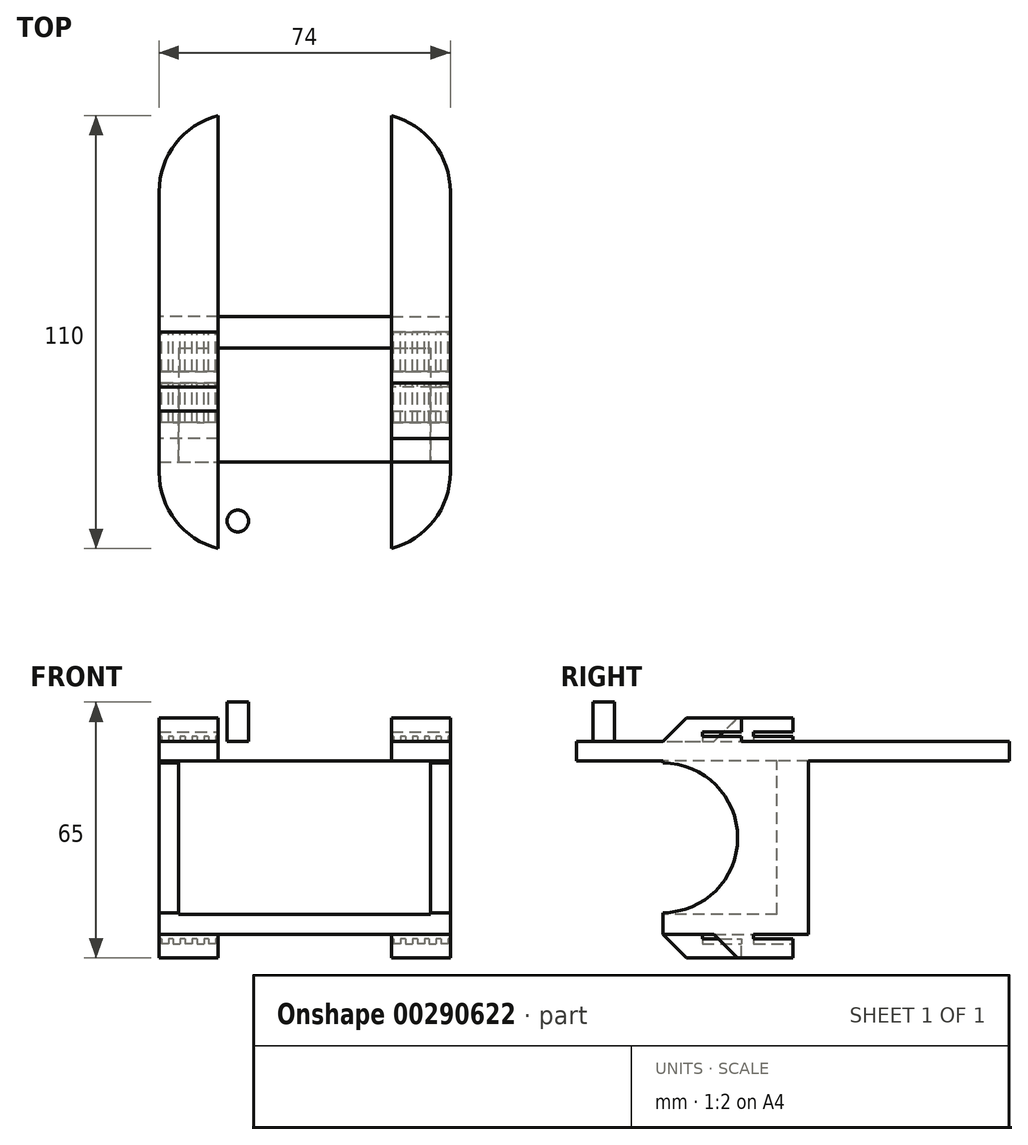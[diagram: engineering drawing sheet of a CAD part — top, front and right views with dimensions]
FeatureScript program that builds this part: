
annotation { "Feature Type Name" : "Feature", "Feature Type Description" : "" }
export const myFeature = defineFeature(function(context is Context, id is Id, definition is map)
    precondition{}
    {
        {
            var Q0;
            Q0=qCreatedBy(makeId("Top.planeOp"),FACE);
            var sketch = newSketch(context, id + "F0", { "sketchPlane" : qUnion([Q0])});
            skLineSegment(sketch, "E0.bottom", {"start": v(-22, 55) * mm, "end": v(22, 55) * mm});
            skLineSegment(sketch, "E0.top", {"start": v(-22, -55) * mm, "end": v(22, -55) * mm});
            skLineSegment(sketch, "E0.left", {"start": v(-22, 55) * mm, "end": v(-22, -55) * mm});
            skLineSegment(sketch, "E0.right", {"start": v(22, 55) * mm, "end": v(22, -55) * mm});
            skLineSegment(sketch, "E1", {"start": v(-22, 0) * mm, "end": v(22, 0) * mm, "construction": true});
            skLineSegment(sketch, "E2", {"start": v(0, 55) * mm, "end": v(0, 25) * mm});
            skPoint(sketch, "E2.endSnap0", {"position": v(0, 55) * mm});
            skLineSegment(sketch, "E3", {"start": v(0, -55) * mm, "end": v(0, -25) * mm});
            skPoint(sketch, "E3.endSnap0", {"position": v(0, -55) * mm});
            skCircle(sketch, "E4", {"center": v(-17, 48) * mm, "radius": 2.75 * mm});
            skLineSegment(sketch, "E5", {"start": v(-22, 30) * mm, "end": v(22, 30) * mm, "construction": true});
            skCircle(sketch, "E6.MirrorC", {"center": v(17, 48) * mm, "radius": 2.75 * mm});
            skCircle(sketch, "E7.MirrorC", {"center": v(-17, 12) * mm, "radius": 2.75 * mm});
            skCircle(sketch, "E8.MirrorC", {"center": v(17, 12) * mm, "radius": 2.75 * mm});
            skCircle(sketch, "E9.MirrorC", {"center": v(-17, -12) * mm, "radius": 2.75 * mm});
            skCircle(sketch, "E10.MirrorC", {"center": v(17, -12) * mm, "radius": 2.75 * mm});
            skCircle(sketch, "E11.MirrorC", {"center": v(17, -48) * mm, "radius": 2.75 * mm});
            skCircle(sketch, "E12.MirrorC", {"center": v(-17, -48) * mm, "radius": 2.75 * mm});
            skSolve(sketch);
        }
        {
            var Q0;
            Q0 = qSketchRegion(id + "F0", true);
            extrude(context, id + "F1", {"entities" : qUnion([Q0]), "depth" : 5 * mm});
        }
        {
            var Q0;
            Q0=makeQuery(id+"F1.opExtrude","CAP_FACE",FACE,{"disambiguationData":[OSD([sQuery(id+"F0.wireOp",EDGE,"E0.bottom"),sQuery(id+"F0.wireOp",EDGE,"E0.top"),sQuery(id+"F0.wireOp",EDGE,"E0.left"),sQuery(id+"F0.wireOp",EDGE,"E0.right")])],"isStart":false});
            var sketch = newSketch(context, id + "F2", { "sketchPlane" : qUnion([Q0])});
            skLineSegment(sketch, "E13.bottom", {"start": v(22, -13) * mm, "end": v(37, -13) * mm});
            skLineSegment(sketch, "E13.top", {"start": v(22, -33) * mm, "end": v(37, -33) * mm});
            skLineSegment(sketch, "E13.left", {"start": v(22, -13) * mm, "end": v(22, -33) * mm});
            skLineSegment(sketch, "E13.right", {"start": v(37, -13) * mm, "end": v(37, -33) * mm});
            skPoint(sketch, "E14.start.orphan", {"position": v(22, 0) * mm});
            skSolve(sketch);
        }
        {
            var Q0;
            Q0 = qSketchRegion(id + "F2", true);
            extrude(context, id + "F3", {"entities" : qUnion([Q0]), "depth" : 6 * mm});
        }
        {
            var Q0;
            Q0=makeQuery(id+"F3.opExtrude","CAP_FACE",FACE,{"disambiguationData":[OSD([sQuery(id+"F2.wireOp",EDGE,"E13.bottom"),sQuery(id+"F2.wireOp",EDGE,"E13.top"),sQuery(id+"F2.wireOp",EDGE,"E13.left"),sQuery(id+"F2.wireOp",EDGE,"E13.right")])],"isStart":true});
            extrude(context, id + "F4", {"entities" : qUnion([Q0]), "operationType" : NewBodyOperationType.ADD, "depth" : 5 * mm});
        }
        {
            var Q0;
            Q0=qCreatedBy(makeId("Top.planeOp"),FACE);
            var sketch = newSketch(context, id + "F5", { "sketchPlane" : qUnion([Q0])});
            skLineSegment(sketch, "E15.bottom", {"start": v(-37, 0) * mm, "end": v(-22, 0) * mm});
            skLineSegment(sketch, "E15.top", {"start": v(-37, -20) * mm, "end": v(-22, -20) * mm});
            skLineSegment(sketch, "E15.left", {"start": v(-37, 0) * mm, "end": v(-37, -20) * mm});
            skLineSegment(sketch, "E15.right", {"start": v(-22, 0) * mm, "end": v(-22, -20) * mm});
            skSolve(sketch);
        }
        {
            var Q0;
            Q0=makeQuery(id+"F5.imprint","IMPRINT",FACE,{"disambiguationData":[TD([[makeQuery(id+"F5.imprint","IMPRINT",EDGE,{"derivedFrom":sQuery(id+"F5.wireOp",EDGE,"E15.bottom")}),-1.0]])]});
            extrude(context, id + "F6", {"entities" : qUnion([Q0]), "operationType" : NewBodyOperationType.ADD, "depth" : 11 * mm});
        }
        {
            var Q0;
            Q0=makeQuery(id+"F6.opExtrude","SWEPT_FACE",FACE,{"disambiguationData":[OSD([sQuery(id+"F5.wireOp",EDGE,"E15.bottom")])]});
            var sketch = newSketch(context, id + "F7", { "sketchPlane" : qUnion([Q0])});
            skPoint(sketch, "E16.start.orphan", {"position": v(22, 6.18) * mm});
            skLineSegment(sketch, "E17", {"start": v(22.6, 5) * mm, "end": v(24.39, 5) * mm});
            skLineSegment(sketch, "E18.MirrorCS", {"start": v(27.4, 5) * mm, "end": v(25.6, 5) * mm});
            skLineSegment(sketch, "E19.MirrorCS", {"start": v(28.6, 5) * mm, "end": v(30.39, 5) * mm});
            skLineSegment(sketch, "E20.MirrorCS", {"start": v(33.4, 5) * mm, "end": v(31.6, 5) * mm});
            skLineSegment(sketch, "E21.MirrorCS", {"start": v(34.6, 5) * mm, "end": v(36.39, 5) * mm});
            skPoint(sketch, "E22.end.orphan", {"position": v(3.35, -0.67) * mm});
            skPoint(sketch, "E23.end.orphan", {"position": v(26.5, 5) * mm});
            skLineSegment(sketch, "E24", {"start": v(36.4, 5) * mm, "end": v(34.6, 5) * mm, "construction": true});
            skLineSegment(sketch, "E25.MirrorCS", {"start": v(36.4, 6.22) * mm, "end": v(37, 6.22) * mm});
            skLineSegment(sketch, "E26.MirrorCS", {"start": v(22, 6.22) * mm, "end": v(22.6, 6.22) * mm});
            skLineSegment(sketch, "E27.MirrorCS", {"start": v(33.4, 6.22) * mm, "end": v(34.6, 6.22) * mm});
            skLineSegment(sketch, "E28.MirrorCS", {"start": v(30.39, 6.22) * mm, "end": v(31.6, 6.22) * mm});
            skLineSegment(sketch, "E29.MirrorCS", {"start": v(24.39, 6.22) * mm, "end": v(25.6, 6.22) * mm});
            skLineSegment(sketch, "E30.MirrorCS", {"start": v(37, 7.4) * mm, "end": v(22, 7.4) * mm});
            skLineSegment(sketch, "E31.MirrorCS", {"start": v(37, 7.4) * mm, "end": v(37, 6.22) * mm});
            skPoint(sketch, "E32.MirrorP", {"position": v(3.35, 10.67) * mm});
            skLineSegment(sketch, "E33.MirrorCS", {"start": v(27.4, 6.22) * mm, "end": v(28.6, 6.22) * mm});
            skLineSegment(sketch, "E34.MirrorCS", {"start": v(22, 7.4) * mm, "end": v(22, 6.22) * mm});
            skLineSegment(sketch, "E35.MirrorCS", {"start": v(36.4, 6.22) * mm, "end": v(36.4, 5) * mm});
            skLineSegment(sketch, "E36.MirrorCS", {"start": v(34.6, 6.22) * mm, "end": v(34.6, 5) * mm});
            skLineSegment(sketch, "E37.MirrorCS", {"start": v(33.4, 6.22) * mm, "end": v(33.4, 5) * mm});
            skLineSegment(sketch, "E38.MirrorCS", {"start": v(31.6, 6.22) * mm, "end": v(31.6, 5) * mm});
            skLineSegment(sketch, "E39.MirrorCS", {"start": v(30.39, 6.22) * mm, "end": v(30.39, 5) * mm});
            skLineSegment(sketch, "E40.MirrorCS", {"start": v(28.6, 6.22) * mm, "end": v(28.6, 5) * mm});
            skLineSegment(sketch, "E41.MirrorCS", {"start": v(25.6, 6.22) * mm, "end": v(25.6, 5) * mm});
            skLineSegment(sketch, "E42.MirrorCS", {"start": v(24.39, 6.22) * mm, "end": v(24.39, 5) * mm});
            skLineSegment(sketch, "E43.MirrorCS", {"start": v(22.6, 6.22) * mm, "end": v(22.6, 5) * mm});
            skLineSegment(sketch, "E44.MirrorCS", {"start": v(27.4, 6.22) * mm, "end": v(27.4, 5) * mm});
            skPoint(sketch, "E45.MirrorCS.end.orphan", {"position": v(36.4, 5) * mm});
            skPoint(sketch, "E46.MirrorCS.end.orphan", {"position": v(34.6, 5) * mm});
            skPoint(sketch, "E47.MirrorCS.end.orphan", {"position": v(33.4, 5) * mm});
            skPoint(sketch, "E48.MirrorCS.end.orphan", {"position": v(31.6, 5) * mm});
            skPoint(sketch, "E49.MirrorCS.end.orphan", {"position": v(30.39, 5) * mm});
            skPoint(sketch, "E50.MirrorCS.end.orphan", {"position": v(28.6, 5) * mm});
            skPoint(sketch, "E51.MirrorCS.end.orphan", {"position": v(27.4, 5) * mm});
            skPoint(sketch, "E52.MirrorCS.end.orphan", {"position": v(25.6, 5) * mm});
            skLineSegment(sketch, "E53.trimOffspring", {"start": v(33.4, 5) * mm, "end": v(31.6, 5) * mm, "construction": true});
            skPoint(sketch, "E54.orphan", {"position": v(37, 5) * mm});
            skLineSegment(sketch, "E55.trimOffspring", {"start": v(30.39, 5) * mm, "end": v(28.6, 5) * mm, "construction": true});
            skLineSegment(sketch, "E56.trimOffspring", {"start": v(27.4, 5) * mm, "end": v(25.6, 5) * mm, "construction": true});
            skLineSegment(sketch, "E57.trimOffspring", {"start": v(24.39, 5) * mm, "end": v(22.6, 5) * mm, "construction": true});
            skLineSegment(sketch, "E58", {"start": v(22, 5) * mm, "end": v(37, 5) * mm});
            skSolve(sketch);
        }
        {
            var Q0;
            {var subQ3=sQuery(id+"F0.wireOp",EDGE,"E0.left");Q0=makeQuery(id+"F0.imprint","IMPRINT",FACE,{"disambiguationData":[TD([[makeQuery(id+"F0.imprint","IMPRINT",EDGE,{"derivedFrom":subQ3}),1.0]])]});}
            var sketch = newSketch(context, id + "F8", { "sketchPlane" : qUnion([Q0])});
            skLineSegment(sketch, "E59.bottom", {"start": v(-22, -4) * mm, "end": v(22, -4) * mm});
            skLineSegment(sketch, "E59.top", {"start": v(-22, 4) * mm, "end": v(22, 4) * mm});
            skLineSegment(sketch, "E59.left", {"start": v(-22, -4) * mm, "end": v(-22, 4) * mm});
            skLineSegment(sketch, "E59.right", {"start": v(22, -4) * mm, "end": v(22, 4) * mm});
            skSolve(sketch);
        }
        {
            var Q0;
            Q0 = qSketchRegion(id + "F8", true);
            extrude(context, id + "F9", {"entities" : qUnion([Q0]), "operationType" : NewBodyOperationType.ADD, "oppositeDirection" : true, "depth" : 39 * mm});
        }
        {
            var Q0;
            Q0=makeQuery(id+"F9.opExtrude","CAP_FACE",FACE,{"disambiguationData":[OSD([sQuery(id+"F8.wireOp",EDGE,"E59.bottom"),sQuery(id+"F8.wireOp",EDGE,"E59.top"),sQuery(id+"F8.wireOp",EDGE,"E59.left"),sQuery(id+"F8.wireOp",EDGE,"E59.right")])],"isStart":false});
            var sketch = newSketch(context, id + "F10", { "sketchPlane" : qUnion([Q0])});
            skLineSegment(sketch, "E60.bottom", {"start": v(22, 20) * mm, "end": v(37, 20) * mm});
            skLineSegment(sketch, "E60.top", {"start": v(22, 0) * mm, "end": v(37, 0) * mm});
            skLineSegment(sketch, "E60.left", {"start": v(22, 20) * mm, "end": v(22, 0) * mm});
            skLineSegment(sketch, "E60.right", {"start": v(37, 20) * mm, "end": v(37, 0) * mm});
            skSolve(sketch);
        }
        {
            var Q0;
            Q0 = qSketchRegion(id + "F10", true);
            extrude(context, id + "F11", {"entities" : qUnion([Q0]), "operationType" : NewBodyOperationType.ADD, "depth" : 11 * mm});
        }
        {
            var Q0;
            Q0=makeQuery(id+"F11.opExtrude","SWEPT_FACE",FACE,{"disambiguationData":[OSD([sQuery(id+"F10.wireOp",EDGE,"E60.top")])]});
            var sketch = newSketch(context, id + "F12", { "sketchPlane" : qUnion([Q0])});
            skLineSegment(sketch, "E61.trimOffspring", {"start": v(-34.6, -47.62) * mm, "end": v(-33.39, -47.62) * mm});
            skLineSegment(sketch, "E62", {"start": v(-36.4, -46.4) * mm, "end": v(-34.6, -46.4) * mm});
            skLineSegment(sketch, "E63.MirrorCS", {"start": v(-31.6, -46.4) * mm, "end": v(-33.39, -46.4) * mm});
            skLineSegment(sketch, "E64.MirrorCS", {"start": v(-30.4, -46.4) * mm, "end": v(-28.6, -46.4) * mm});
            skLineSegment(sketch, "E65.MirrorCS", {"start": v(-25.6, -46.4) * mm, "end": v(-27.39, -46.4) * mm});
            skLineSegment(sketch, "E66.MirrorCS", {"start": v(-24.4, -46.4) * mm, "end": v(-22.6, -46.4) * mm});
            skPoint(sketch, "E67.end.orphan", {"position": v(-25.06, -46.93) * mm});
            skPoint(sketch, "E68.end.orphan", {"position": v(-32.5, -46.4) * mm});
            skLineSegment(sketch, "E69", {"start": v(-22.6, -46.4) * mm, "end": v(-24.4, -46.4) * mm, "construction": true});
            skLineSegment(sketch, "E70.MirrorCS", {"start": v(-22.6, -45.18) * mm, "end": v(-22, -45.18) * mm});
            skLineSegment(sketch, "E71.MirrorCS", {"start": v(-37, -45.18) * mm, "end": v(-36.4, -45.18) * mm});
            skLineSegment(sketch, "E72.MirrorCS", {"start": v(-25.6, -45.18) * mm, "end": v(-24.4, -45.18) * mm});
            skLineSegment(sketch, "E73.MirrorCS", {"start": v(-28.6, -45.18) * mm, "end": v(-27.39, -45.18) * mm});
            skLineSegment(sketch, "E74.MirrorCS", {"start": v(-34.6, -45.18) * mm, "end": v(-33.39, -45.18) * mm});
            skLineSegment(sketch, "E75.MirrorCS", {"start": v(-22, -44) * mm, "end": v(-37, -44) * mm});
            skLineSegment(sketch, "E76.MirrorCS", {"start": v(-22, -44) * mm, "end": v(-22, -45.18) * mm});
            skPoint(sketch, "E77.MirrorP", {"position": v(-25.06, -45.87) * mm});
            skLineSegment(sketch, "E78.MirrorCS", {"start": v(-31.6, -45.18) * mm, "end": v(-30.4, -45.18) * mm});
            skLineSegment(sketch, "E79.MirrorCS", {"start": v(-37, -44) * mm, "end": v(-37, -45.18) * mm});
            skLineSegment(sketch, "E80.MirrorCS", {"start": v(-22.6, -45.18) * mm, "end": v(-22.6, -46.4) * mm});
            skLineSegment(sketch, "E81.MirrorCS", {"start": v(-24.4, -45.18) * mm, "end": v(-24.4, -46.4) * mm});
            skLineSegment(sketch, "E82.MirrorCS", {"start": v(-25.6, -45.18) * mm, "end": v(-25.6, -46.4) * mm});
            skLineSegment(sketch, "E83.MirrorCS", {"start": v(-27.39, -45.18) * mm, "end": v(-27.39, -46.4) * mm});
            skLineSegment(sketch, "E84.MirrorCS", {"start": v(-28.6, -45.18) * mm, "end": v(-28.6, -46.4) * mm});
            skLineSegment(sketch, "E85.MirrorCS", {"start": v(-30.4, -45.18) * mm, "end": v(-30.4, -46.4) * mm});
            skLineSegment(sketch, "E86.MirrorCS", {"start": v(-33.39, -45.18) * mm, "end": v(-33.39, -46.4) * mm});
            skLineSegment(sketch, "E87.MirrorCS", {"start": v(-34.6, -45.18) * mm, "end": v(-34.6, -46.4) * mm});
            skLineSegment(sketch, "E88.MirrorCS", {"start": v(-36.4, -45.18) * mm, "end": v(-36.4, -46.4) * mm});
            skLineSegment(sketch, "E89.MirrorCS", {"start": v(-31.6, -45.18) * mm, "end": v(-31.6, -46.4) * mm});
            skPoint(sketch, "E90.end.orphan", {"position": v(-36.4, -47.62) * mm});
            skPoint(sketch, "E90.start.orphan", {"position": v(-37, -47.62) * mm});
            skPoint(sketch, "E91.end.orphan", {"position": v(-37, -48.8) * mm});
            skPoint(sketch, "E92.start.orphan", {"position": v(-22, -48.8) * mm});
            skPoint(sketch, "E93.trimOffspring.end.orphan", {"position": v(-22, -47.62) * mm});
            skPoint(sketch, "E94.MirrorCS.end.orphan", {"position": v(-22.6, -46.4) * mm});
            skPoint(sketch, "E94.MirrorCS.start.orphan", {"position": v(-22.6, -47.62) * mm});
            skPoint(sketch, "E95.MirrorCS.end.orphan", {"position": v(-24.4, -46.4) * mm});
            skPoint(sketch, "E96.MirrorCS.end.orphan", {"position": v(-25.6, -46.4) * mm});
            skPoint(sketch, "E97.MirrorCS.end.orphan", {"position": v(-27.39, -46.4) * mm});
            skPoint(sketch, "E98.MirrorCS.end.orphan", {"position": v(-28.6, -46.4) * mm});
            skPoint(sketch, "E99.trimOffspring.end.orphan", {"position": v(-27.39, -47.62) * mm});
            skPoint(sketch, "E99.trimOffspring.start.orphan", {"position": v(-28.6, -47.62) * mm});
            skPoint(sketch, "E100.orphan", {"position": v(-25.6, -47.62) * mm});
            skPoint(sketch, "E101.trimOffspring.end.orphan", {"position": v(-24.4, -47.62) * mm});
            skPoint(sketch, "E102.MirrorCS.end.orphan", {"position": v(-30.4, -46.4) * mm});
            skPoint(sketch, "E103.MirrorCS.end.orphan", {"position": v(-31.6, -46.4) * mm});
            skPoint(sketch, "E104.trimOffspring.end.orphan", {"position": v(-30.4, -47.62) * mm});
            skPoint(sketch, "E104.trimOffspring.start.orphan", {"position": v(-31.6, -47.62) * mm});
            skPoint(sketch, "E105.MirrorCS.end.orphan", {"position": v(-33.39, -46.4) * mm});
            skLineSegment(sketch, "E106.trimOffspring", {"start": v(-25.6, -46.4) * mm, "end": v(-27.39, -46.4) * mm, "construction": true});
            skPoint(sketch, "E107.orphan", {"position": v(-22, -46.4) * mm});
            skLineSegment(sketch, "E108.trimOffspring", {"start": v(-28.6, -46.4) * mm, "end": v(-30.4, -46.4) * mm, "construction": true});
            skLineSegment(sketch, "E109.trimOffspring", {"start": v(-31.6, -46.4) * mm, "end": v(-33.39, -46.4) * mm, "construction": true});
            skLineSegment(sketch, "E110.trimOffspring", {"start": v(-34.6, -46.4) * mm, "end": v(-36.4, -46.4) * mm, "construction": true});
            skSolve(sketch);
        }
        {
            var Q0;
            Q0=makeQuery(id+"F9.opExtrude","CAP_FACE",FACE,{"disambiguationData":[OSD([sQuery(id+"F8.wireOp",EDGE,"E59.bottom"),sQuery(id+"F8.wireOp",EDGE,"E59.top"),sQuery(id+"F8.wireOp",EDGE,"E59.left"),sQuery(id+"F8.wireOp",EDGE,"E59.right")])],"isStart":false});
            var sketch = newSketch(context, id + "F13", { "sketchPlane" : qUnion([Q0])});
            skLineSegment(sketch, "E111.bottom", {"start": v(22, -4) * mm, "end": v(-22, -4) * mm});
            skLineSegment(sketch, "E111.top", {"start": v(22, 33) * mm, "end": v(-22, 33) * mm});
            skLineSegment(sketch, "E111.left", {"start": v(22, -4) * mm, "end": v(22, 33) * mm});
            skLineSegment(sketch, "E111.right", {"start": v(-22, -4) * mm, "end": v(-22, 33) * mm});
            skLineSegment(sketch, "E112.bottom", {"start": v(22, -4) * mm, "end": v(37, -4) * mm});
            skLineSegment(sketch, "E112.top", {"start": v(22, 33) * mm, "end": v(37, 33) * mm});
            skLineSegment(sketch, "E112.right", {"start": v(37, -4) * mm, "end": v(37, 33) * mm});
            skLineSegment(sketch, "E113.bottom", {"start": v(-22, -4) * mm, "end": v(-37, -4) * mm});
            skLineSegment(sketch, "E113.top", {"start": v(-22, 33) * mm, "end": v(-37, 33) * mm});
            skLineSegment(sketch, "E113.right", {"start": v(-37, -4) * mm, "end": v(-37, 33) * mm});
            skSolve(sketch);
        }
        {
            var Q0;
            Q0 = qSketchRegion(id + "F13", true);
            extrude(context, id + "F14", {"entities" : qUnion([Q0]), "operationType" : NewBodyOperationType.ADD, "depth" : 5 * mm});
        }
        {
            var Q0;
            Q0=makeQuery(id+"F12.imprint","IMPRINT",FACE,{"disambiguationData":[TD([[makeQuery(id+"F12.imprint","IMPRINT",EDGE,{"derivedFrom":sQuery(id+"F12.wireOp",EDGE,"E62")}),1.0]])]});
            extrude(context, id + "F15", {"entities" : qUnion([Q0]), "operationType" : NewBodyOperationType.REMOVE, "oppositeDirection" : true, "depth" : 10 * mm});
        }
        {
            var Q0;
            Q0=makeQuery(id+"F15.boolean.opBoolean","MERGE",FACE,{"derivedFrom":[makeQuery(id+"F14.opExtrude","CAP_FACE",FACE,{"disambiguationData":[OSD([sQuery(id+"F13.wireOp",EDGE,"E111.bottom"),sQuery(id+"F13.wireOp",EDGE,"E111.top"),sQuery(id+"F13.wireOp",EDGE,"E111.left"),sQuery(id+"F13.wireOp",EDGE,"E111.right")])],"isStart":false}),makeQuery(id+"F15.opExtrude","SWEPT_FACE",FACE,{"disambiguationData":[OSD([sQuery(id+"F12.wireOp",EDGE,"E75.MirrorCS")])]})]});
            var sketch = newSketch(context, id + "F16", { "sketchPlane" : qUnion([Q0])});
            skLineSegment(sketch, "E114.bottom", {"start": v(-37, 33) * mm, "end": v(-22, 33) * mm});
            skLineSegment(sketch, "E114.top", {"start": v(-37, 13) * mm, "end": v(-22, 13) * mm});
            skLineSegment(sketch, "E114.left", {"start": v(-37, 33) * mm, "end": v(-37, 13) * mm});
            skLineSegment(sketch, "E114.right", {"start": v(-22, 33) * mm, "end": v(-22, 13) * mm});
            skSolve(sketch);
        }
        {
            var Q0;
            Q0=makeQuery(id+"F16.imprint","IMPRINT",FACE,{"disambiguationData":[TD([[makeQuery(id+"F16.imprint","IMPRINT",EDGE,{"derivedFrom":sQuery(id+"F16.wireOp",EDGE,"E114.bottom")}),-1.0]])]});
            extrude(context, id + "F17", {"entities" : qUnion([Q0]), "depth" : 6 * mm});
        }
        {
            var Q0;
            Q0=makeQuery(id+"F17.opExtrude","CAP_FACE",FACE,{"disambiguationData":[OSD([sQuery(id+"F16.wireOp",EDGE,"E114.bottom"),sQuery(id+"F16.wireOp",EDGE,"E114.top"),sQuery(id+"F16.wireOp",EDGE,"E114.left"),sQuery(id+"F16.wireOp",EDGE,"E114.right")])],"isStart":true});
            extrude(context, id + "F18", {"entities" : qUnion([Q0]), "operationType" : NewBodyOperationType.ADD, "depth" : 5 * mm});
        }
        {
            var Q0;
            {var subQ0=sQuery(id+"F16.wireOp",EDGE,"E114.top");Q0=makeQuery(id+"F18.boolean.opBoolean","MERGE",FACE,{"derivedFrom":[makeQuery(id+"F17.opExtrude","SWEPT_FACE",FACE,{"disambiguationData":[OSD([subQ0])]}),makeQuery(id+"F18.opExtrude","SWEPT_FACE",FACE,{"disambiguationData":[OSD([subQ0])]})]});}
            var sketch = newSketch(context, id + "F19", { "sketchPlane" : qUnion([Q0])});
            skLineSegment(sketch, "E115.trimOffspring", {"start": v(24.39, -47.62) * mm, "end": v(25.6, -47.62) * mm});
            skLineSegment(sketch, "E116", {"start": v(22.6, -46.4) * mm, "end": v(24.39, -46.4) * mm});
            skLineSegment(sketch, "E117.MirrorCS", {"start": v(27.4, -46.4) * mm, "end": v(25.6, -46.4) * mm});
            skLineSegment(sketch, "E118.MirrorCS", {"start": v(28.6, -46.4) * mm, "end": v(30.39, -46.4) * mm});
            skLineSegment(sketch, "E119.MirrorCS", {"start": v(33.4, -46.4) * mm, "end": v(31.6, -46.4) * mm});
            skLineSegment(sketch, "E120.MirrorCS", {"start": v(34.6, -46.4) * mm, "end": v(36.39, -46.4) * mm});
            skPoint(sketch, "E121.end.orphan", {"position": v(33.38, -47.05) * mm});
            skPoint(sketch, "E122.end.orphan", {"position": v(26.5, -46.4) * mm});
            skLineSegment(sketch, "E123", {"start": v(36.4, -46.4) * mm, "end": v(34.6, -46.4) * mm, "construction": true});
            skLineSegment(sketch, "E124.MirrorCS", {"start": v(36.4, -45.18) * mm, "end": v(37, -45.18) * mm});
            skLineSegment(sketch, "E125.MirrorCS", {"start": v(22, -45.18) * mm, "end": v(22.6, -45.18) * mm});
            skLineSegment(sketch, "E126.MirrorCS", {"start": v(33.4, -45.18) * mm, "end": v(34.6, -45.18) * mm});
            skLineSegment(sketch, "E127.MirrorCS", {"start": v(30.39, -45.18) * mm, "end": v(31.6, -45.18) * mm});
            skLineSegment(sketch, "E128.MirrorCS", {"start": v(24.39, -45.18) * mm, "end": v(25.6, -45.18) * mm});
            skLineSegment(sketch, "E129.MirrorCS", {"start": v(37, -44) * mm, "end": v(22, -44) * mm});
            skLineSegment(sketch, "E130.MirrorCS", {"start": v(37, -44) * mm, "end": v(37, -45.18) * mm});
            skPoint(sketch, "E131.MirrorP", {"position": v(33.38, -45.75) * mm});
            skLineSegment(sketch, "E132.MirrorCS", {"start": v(27.4, -45.18) * mm, "end": v(28.6, -45.18) * mm});
            skLineSegment(sketch, "E133.MirrorCS", {"start": v(22, -44) * mm, "end": v(22, -45.18) * mm});
            skLineSegment(sketch, "E134.MirrorCS", {"start": v(36.4, -45.18) * mm, "end": v(36.4, -46.4) * mm});
            skLineSegment(sketch, "E135.MirrorCS", {"start": v(34.6, -45.18) * mm, "end": v(34.6, -46.4) * mm});
            skLineSegment(sketch, "E136.MirrorCS", {"start": v(33.4, -45.18) * mm, "end": v(33.4, -46.4) * mm});
            skLineSegment(sketch, "E137.MirrorCS", {"start": v(31.6, -45.18) * mm, "end": v(31.6, -46.4) * mm});
            skLineSegment(sketch, "E138.MirrorCS", {"start": v(30.39, -45.18) * mm, "end": v(30.39, -46.4) * mm});
            skLineSegment(sketch, "E139.MirrorCS", {"start": v(28.6, -45.18) * mm, "end": v(28.6, -46.4) * mm});
            skLineSegment(sketch, "E140.MirrorCS", {"start": v(25.6, -45.18) * mm, "end": v(25.6, -46.4) * mm});
            skLineSegment(sketch, "E141.MirrorCS", {"start": v(24.39, -45.18) * mm, "end": v(24.39, -46.4) * mm});
            skLineSegment(sketch, "E142.MirrorCS", {"start": v(22.6, -45.18) * mm, "end": v(22.6, -46.4) * mm});
            skLineSegment(sketch, "E143.MirrorCS", {"start": v(27.4, -45.18) * mm, "end": v(27.4, -46.4) * mm});
            skPoint(sketch, "E144.end.orphan", {"position": v(22.6, -47.62) * mm});
            skPoint(sketch, "E144.start.orphan", {"position": v(22, -47.62) * mm});
            skPoint(sketch, "E145.end.orphan", {"position": v(22, -48.8) * mm});
            skPoint(sketch, "E146.start.orphan", {"position": v(37, -48.8) * mm});
            skPoint(sketch, "E147.trimOffspring.end.orphan", {"position": v(37, -47.62) * mm});
            skPoint(sketch, "E148.MirrorCS.end.orphan", {"position": v(36.4, -46.4) * mm});
            skPoint(sketch, "E148.MirrorCS.start.orphan", {"position": v(36.4, -47.62) * mm});
            skPoint(sketch, "E149.MirrorCS.end.orphan", {"position": v(34.6, -46.4) * mm});
            skPoint(sketch, "E150.MirrorCS.end.orphan", {"position": v(33.4, -46.4) * mm});
            skPoint(sketch, "E151.MirrorCS.end.orphan", {"position": v(31.6, -46.4) * mm});
            skPoint(sketch, "E152.MirrorCS.end.orphan", {"position": v(30.39, -46.4) * mm});
            skPoint(sketch, "E153.trimOffspring.end.orphan", {"position": v(31.6, -47.62) * mm});
            skPoint(sketch, "E153.trimOffspring.start.orphan", {"position": v(30.39, -47.62) * mm});
            skPoint(sketch, "E154.orphan", {"position": v(33.4, -47.62) * mm});
            skPoint(sketch, "E155.trimOffspring.end.orphan", {"position": v(34.6, -47.62) * mm});
            skPoint(sketch, "E156.MirrorCS.end.orphan", {"position": v(28.6, -46.4) * mm});
            skPoint(sketch, "E157.MirrorCS.end.orphan", {"position": v(27.4, -46.4) * mm});
            skPoint(sketch, "E158.trimOffspring.end.orphan", {"position": v(28.6, -47.62) * mm});
            skPoint(sketch, "E158.trimOffspring.start.orphan", {"position": v(27.4, -47.62) * mm});
            skPoint(sketch, "E159.MirrorCS.end.orphan", {"position": v(25.6, -46.4) * mm});
            skLineSegment(sketch, "E160.trimOffspring", {"start": v(33.4, -46.4) * mm, "end": v(31.6, -46.4) * mm, "construction": true});
            skPoint(sketch, "E161.orphan", {"position": v(37, -46.4) * mm});
            skLineSegment(sketch, "E162.trimOffspring", {"start": v(30.39, -46.4) * mm, "end": v(28.6, -46.4) * mm, "construction": true});
            skLineSegment(sketch, "E163.trimOffspring", {"start": v(27.4, -46.4) * mm, "end": v(25.6, -46.4) * mm, "construction": true});
            skLineSegment(sketch, "E164.trimOffspring", {"start": v(24.39, -46.4) * mm, "end": v(22.6, -46.4) * mm, "construction": true});
            skSolve(sketch);
        }
        {
            var Q0;
            Q0=makeQuery(id+"F19.imprint","IMPRINT",FACE,{"disambiguationData":[TD([[makeQuery(id+"F19.imprint","IMPRINT",EDGE,{"derivedFrom":sQuery(id+"F19.wireOp",EDGE,"E116")}),1.0]])]});
            extrude(context, id + "F20", {"entities" : qUnion([Q0]), "operationType" : NewBodyOperationType.REMOVE, "oppositeDirection" : true, "depth" : 10 * mm});
        }
        {
            var Q0;
            Q0=makeQuery(id+"F6.opExtrude","CAP_EDGE",EDGE,{"disambiguationData":[OSD([sQuery(id+"F5.wireOp",EDGE,"E15.top")])],"isStart":false});
            var Q1;
            Q1=makeQuery(id+"F3.opExtrude","CAP_EDGE",EDGE,{"disambiguationData":[OSD([sQuery(id+"F2.wireOp",EDGE,"E13.top")])],"isStart":false});
            var Q2;
            Q2=makeQuery(id+"F11.opExtrude","CAP_EDGE",EDGE,{"disambiguationData":[OSD([sQuery(id+"F10.wireOp",EDGE,"E60.bottom")])],"isStart":false});
            var Q3;
            Q3=makeQuery(id+"F17.opExtrude","CAP_EDGE",EDGE,{"disambiguationData":[OSD([sQuery(id+"F16.wireOp",EDGE,"E114.bottom")])],"isStart":false});
            chamfer(context, id + "F21", {"entities" : qUnion([Q0, Q1, Q2, Q3]), "width" : 6 * mm, "tangentPropagation" : true});
        }
        {
            var Q0;
            Q0=qCreatedBy(makeId("Top.planeOp"),FACE);
            var sketch = newSketch(context, id + "F22", { "sketchPlane" : qUnion([Q0])});
            skLineSegment(sketch, "E165.bottom", {"start": v(37, 4) * mm, "end": v(22, 4) * mm});
            skLineSegment(sketch, "E165.top", {"start": v(37, -13) * mm, "end": v(22, -13) * mm});
            skLineSegment(sketch, "E165.left", {"start": v(37, 4) * mm, "end": v(37, -13) * mm});
            skLineSegment(sketch, "E165.right", {"start": v(22, 4) * mm, "end": v(22, -13) * mm});
            skLineSegment(sketch, "E166.bottom", {"start": v(-37, -33) * mm, "end": v(-22, -33) * mm});
            skLineSegment(sketch, "E166.top", {"start": v(-37, -20) * mm, "end": v(-22, -20) * mm});
            skLineSegment(sketch, "E166.left", {"start": v(-37, -33) * mm, "end": v(-37, -20) * mm});
            skLineSegment(sketch, "E166.right", {"start": v(-22, -33) * mm, "end": v(-22, -20) * mm});
            skLineSegment(sketch, "E167.bottom", {"start": v(-37, 4) * mm, "end": v(-22, 4) * mm});
            skLineSegment(sketch, "E167.top", {"start": v(-37, 0) * mm, "end": v(-22, 0) * mm});
            skLineSegment(sketch, "E167.left", {"start": v(-37, 4) * mm, "end": v(-37, 0) * mm});
            skLineSegment(sketch, "E167.right", {"start": v(-22, 4) * mm, "end": v(-22, 0) * mm});
            skSolve(sketch);
        }
        {
            var Q0;
            Q0=makeQuery(id+"F22.imprint","IMPRINT",FACE,{"disambiguationData":[TD([[makeQuery(id+"F22.imprint","IMPRINT",EDGE,{"derivedFrom":sQuery(id+"F22.wireOp",EDGE,"E166.bottom")}),1.0]])]});
            var Q1;
            Q1=makeQuery(id+"F22.imprint","IMPRINT",FACE,{"disambiguationData":[TD([[makeQuery(id+"F22.imprint","IMPRINT",EDGE,{"derivedFrom":sQuery(id+"F22.wireOp",EDGE,"E167.bottom")}),-1.0]])]});
            var Q2;
            Q2=makeQuery(id+"F22.imprint","IMPRINT",FACE,{"disambiguationData":[TD([[makeQuery(id+"F22.imprint","IMPRINT",EDGE,{"derivedFrom":sQuery(id+"F22.wireOp",EDGE,"E165.bottom")}),1.0]])]});
            var Q3;
            Q3 = qConstructionFilter(qBodyType(qCreatedBy(id + "F22" ,EDGE), BodyType.WIRE), ConstructionObject.NO);
            extrude(context, id + "F23", {"entities" : qUnion([Q0, Q1, Q2]), "operationType" : NewBodyOperationType.ADD, "surfaceEntities" : qUnion([Q3]), "depth" : 5 * mm});
        }
        {
            var Q0;
            {var subQ0=sQuery(id+"F2.wireOp",EDGE,"E13.bottom");var subQ1=sQuery(id+"F5.wireOp",EDGE,"E15.bottom");var subQ2=sQuery(id+"F2.wireOp",EDGE,"E13.right");var subQ3=sQuery(id+"F2.wireOp",EDGE,"E13.top");var subQ4=sQuery(id+"F0.wireOp",EDGE,"E0.left");var subQ5=sQuery(id+"F0.wireOp",EDGE,"E0.top");var subQ6=sQuery(id+"F0.wireOp",EDGE,"E0.right");var subQ7=sQuery(id+"F5.wireOp",EDGE,"E15.top");var subQ8=sQuery(id+"F5.wireOp",EDGE,"E15.left");Q0=makeQuery(id+"F23.boolean.opBoolean","MERGE",FACE,{"derivedFrom":[makeQuery(id+"F9.boolean.opBoolean","SPLIT",FACE,{"disambiguationData":[TD([makeQuery(id+"F1.opExtrude","SWEPT_FACE",FACE,{"disambiguationData":[OSD([subQ5])]})])],"derivedFrom":makeQuery(id+"F6.boolean.opBoolean","MERGE",FACE,{"derivedFrom":[makeQuery(id+"F4.boolean.opBoolean","MERGE",FACE,{"derivedFrom":[makeQuery(id+"F1.opExtrude","CAP_FACE",FACE,{"disambiguationData":[OSD([sQuery(id+"F0.wireOp",EDGE,"E0.bottom"),subQ5,subQ4,subQ6])],"isStart":true}),makeQuery(id+"F4.opExtrude","CAP_FACE",FACE,{"disambiguationData":[OSD([subQ0,subQ3,sQuery(id+"F2.wireOp",EDGE,"E13.left"),subQ2])],"isStart":false})]}),makeQuery(id+"F6.opExtrude","CAP_FACE",FACE,{"disambiguationData":[OSD([subQ1,subQ7,subQ8,sQuery(id+"F5.wireOp",EDGE,"E15.right")])],"isStart":true})]})}),makeQuery(id+"F23.opExtrude","CAP_FACE",FACE,{"disambiguationData":[OSD([sQuery(id+"F22.wireOp",EDGE,"E165.bottom"),sQuery(id+"F22.wireOp",EDGE,"E165.top"),sQuery(id+"F22.wireOp",EDGE,"E165.left"),sQuery(id+"F22.wireOp",EDGE,"E165.right")])],"isStart":true}),makeQuery(id+"F23.opExtrude","CAP_FACE",FACE,{"disambiguationData":[OSD([sQuery(id+"F22.wireOp",EDGE,"E166.bottom"),sQuery(id+"F22.wireOp",EDGE,"E166.top"),sQuery(id+"F22.wireOp",EDGE,"E166.left"),sQuery(id+"F22.wireOp",EDGE,"E166.right")])],"isStart":true}),makeQuery(id+"F23.opExtrude","CAP_FACE",FACE,{"disambiguationData":[OSD([sQuery(id+"F22.wireOp",EDGE,"E167.bottom"),sQuery(id+"F22.wireOp",EDGE,"E167.top"),sQuery(id+"F22.wireOp",EDGE,"E167.left"),sQuery(id+"F22.wireOp",EDGE,"E167.right")])],"isStart":true})]});}
            var sketch = newSketch(context, id + "F24", { "sketchPlane" : qUnion([Q0])});
            skLineSegment(sketch, "E168.bottom", {"start": v(37, -4) * mm, "end": v(32, -4) * mm});
            skLineSegment(sketch, "E168.top", {"start": v(37, 33) * mm, "end": v(32, 33) * mm});
            skLineSegment(sketch, "E168.left", {"start": v(37, -4) * mm, "end": v(37, 33) * mm});
            skLineSegment(sketch, "E168.right", {"start": v(32, -4) * mm, "end": v(32, 33) * mm});
            skLineSegment(sketch, "E169.bottom", {"start": v(-37, -4) * mm, "end": v(-32, -4) * mm});
            skLineSegment(sketch, "E169.top", {"start": v(-37, 33) * mm, "end": v(-32, 33) * mm});
            skLineSegment(sketch, "E169.left", {"start": v(-37, -4) * mm, "end": v(-37, 33) * mm});
            skLineSegment(sketch, "E169.right", {"start": v(-32, -4) * mm, "end": v(-32, 33) * mm});
            skLineSegment(sketch, "E170.bottom", {"start": v(-32, -4) * mm, "end": v(-22, -4) * mm});
            skLineSegment(sketch, "E170.top", {"start": v(-32, 4) * mm, "end": v(-22, 4) * mm});
            skLineSegment(sketch, "E170.left", {"start": v(-32, -4) * mm, "end": v(-32, 4) * mm});
            skLineSegment(sketch, "E170.right", {"start": v(-22, -4) * mm, "end": v(-22, 4) * mm});
            skLineSegment(sketch, "E171.bottom", {"start": v(22, 4) * mm, "end": v(32, 4) * mm});
            skLineSegment(sketch, "E171.top", {"start": v(22, -4) * mm, "end": v(32, -4) * mm});
            skLineSegment(sketch, "E171.left", {"start": v(22, 4) * mm, "end": v(22, -4) * mm});
            skLineSegment(sketch, "E171.right", {"start": v(32, 4) * mm, "end": v(32, -4) * mm});
            skSolve(sketch);
        }
        {
            var Q0;
            Q0 = qSketchRegion(id + "F24", true);
            extrude(context, id + "F25", {"entities" : qUnion([Q0]), "operationType" : NewBodyOperationType.ADD, "depth" : 39 * mm});
        }
        {
            var Q0;
            Q0=makeQuery(id+"F7.imprint","IMPRINT",FACE,{"disambiguationData":[TD([[makeQuery(id+"F7.imprint","IMPRINT",EDGE,{"derivedFrom":sQuery(id+"F7.wireOp",EDGE,"E25.MirrorCS")}),1.0]])]});
            extrude(context, id + "F26", {"entities" : qUnion([Q0]), "operationType" : NewBodyOperationType.REMOVE, "oppositeDirection" : true, "depth" : 10 * mm});
        }
        {
            var Q0;
            Q0=makeQuery(id+"F23.boolean.opBoolean","MERGE",FACE,{"derivedFrom":[makeQuery(id+"F26.boolean.opBoolean","MERGE",FACE,{"derivedFrom":[makeQuery(id+"FRn4Qe3DFnezeeS_1.boolean.opBoolean","MERGE",FACE,{"derivedFrom":[makeQuery(id+"F1.opExtrude","CAP_FACE",FACE,{"disambiguationData":[OSD([sQuery(id+"F0.wireOp",EDGE,"E0.bottom"),sQuery(id+"F0.wireOp",EDGE,"E0.top"),sQuery(id+"F0.wireOp",EDGE,"E0.left"),sQuery(id+"F0.wireOp",EDGE,"E0.right"),sQuery(id+"F0.wireOp",EDGE,"E4"),sQuery(id+"F0.wireOp",EDGE,"E6.MirrorC"),sQuery(id+"F0.wireOp",EDGE,"E7.MirrorC"),sQuery(id+"F0.wireOp",EDGE,"E8.MirrorC"),sQuery(id+"F0.wireOp",EDGE,"E9.MirrorC"),sQuery(id+"F0.wireOp",EDGE,"E10.MirrorC"),sQuery(id+"F0.wireOp",EDGE,"E11.MirrorC"),sQuery(id+"F0.wireOp",EDGE,"E12.MirrorC")])],"isStart":false}),makeQuery(id+"FRn4Qe3DFnezeeS_1.opExtrude","SWEPT_FACE",FACE,{"disambiguationData":[OSD([sQuery(id+"FIRUwi0kTnHVQPe_1.wireOp",EDGE,"PMGgYY30-C1F5-1e5P-kKTP-dWcDxOdKitEs")])]})]}),makeQuery(id+"F26.opExtrude","SWEPT_FACE",FACE,{"disambiguationData":[OSD([sQuery(id+"F7.wireOp",EDGE,"e143cd28-05bc-4d29-98b0-aba1b0c45d87")])]})]}),makeQuery(id+"F23.opExtrude","CAP_FACE",FACE,{"disambiguationData":[OSD([sQuery(id+"F22.wireOp",EDGE,"E165.bottom"),sQuery(id+"F22.wireOp",EDGE,"E165.top"),sQuery(id+"F22.wireOp",EDGE,"E165.left"),sQuery(id+"F22.wireOp",EDGE,"E165.right")])],"isStart":false}),makeQuery(id+"F23.opExtrude","CAP_FACE",FACE,{"disambiguationData":[OSD([sQuery(id+"F22.wireOp",EDGE,"E166.bottom"),sQuery(id+"F22.wireOp",EDGE,"E166.top"),sQuery(id+"F22.wireOp",EDGE,"E166.left"),sQuery(id+"F22.wireOp",EDGE,"E166.right")])],"isStart":false}),makeQuery(id+"F23.opExtrude","CAP_FACE",FACE,{"disambiguationData":[OSD([sQuery(id+"F22.wireOp",EDGE,"E167.bottom"),sQuery(id+"F22.wireOp",EDGE,"E167.top"),sQuery(id+"F22.wireOp",EDGE,"E167.left"),sQuery(id+"F22.wireOp",EDGE,"E167.right")])],"isStart":false})]});
            var sketch = newSketch(context, id + "F27", { "sketchPlane" : qUnion([Q0])});
            skLineSegment(sketch, "E172.bottom", {"start": v(-22, -55) * mm, "end": v(22, -55) * mm});
            skLineSegment(sketch, "E172.top", {"start": v(-22, -41) * mm, "end": v(22, -41) * mm});
            skLineSegment(sketch, "E172.left", {"start": v(-22, -55) * mm, "end": v(-22, -41) * mm});
            skLineSegment(sketch, "E172.right", {"start": v(22, -55) * mm, "end": v(22, -41) * mm});
            skSolve(sketch);
        }
        {
            var Q0;
            Q0 = qSketchRegion(id + "F27", true);
            extrude(context, id + "F28", {"entities" : qUnion([Q0]), "operationType" : NewBodyOperationType.ADD, "depth" : 10 * mm});
        }
        {
            var Q0;
            Q0=makeQuery(id+"F28.opExtrude","SWEPT_FACE",FACE,{"disambiguationData":[OSD([sQuery(id+"F27.wireOp",EDGE,"E172.top")])]});
            var sketch = newSketch(context, id + "F29", { "sketchPlane" : qUnion([Q0])});
            skCircle(sketch, "E173", {"center": v(0, 15) * mm, "radius": 6 * mm});
            skSolve(sketch);
        }
        {
            var Q0;
            {var subQ0=sQuery(id+"F29.wireOp",EDGE,"E173");var subQ1=makeQuery(id+"F28.opExtrude","CAP_EDGE",EDGE,{"disambiguationData":[OSD([sQuery(id+"F27.wireOp",EDGE,"E172.top")])],"isStart":false});var subQ2=makeQuery(id+"F29.imprint","INTERSECT",VERTEX,{"disambiguationData":[OD(0.0)],"derivedFrom":[subQ1,subQ0]});Q0=makeQuery(id+"F29.imprint","IMPRINT",FACE,{"disambiguationData":[TD([[makeQuery(id+"F29.imprint","IMPRINT",EDGE,{"disambiguationData":[TD([[subQ2,-1.0]])],"derivedFrom":subQ0}),1.0]])]});}
            var Q1;
            {var subQ0=sQuery(id+"F29.wireOp",EDGE,"E173");var subQ1=makeQuery(id+"F28.opExtrude","CAP_EDGE",EDGE,{"disambiguationData":[OSD([sQuery(id+"F27.wireOp",EDGE,"E172.top")])],"isStart":false});var subQ2=makeQuery(id+"F29.imprint","INTERSECT",VERTEX,{"disambiguationData":[OD(0.0)],"derivedFrom":[subQ1,subQ0]});Q1=makeQuery(id+"F29.imprint","IMPRINT",FACE,{"disambiguationData":[TD([[makeQuery(id+"F29.imprint","IMPRINT",EDGE,{"disambiguationData":[TD([[subQ2,1.0]])],"derivedFrom":subQ0}),1.0]])]});}
            extrude(context, id + "F30", {"entities" : qUnion([Q0, Q1]), "operationType" : NewBodyOperationType.REMOVE, "oppositeDirection" : true, "depth" : 14 * mm});
        }
        {
            var Q0;
            Q0=makeQuery(id+"F0.imprint","IMPRINT",FACE,{"disambiguationData":[TD([[makeQuery(id+"F0.imprint","IMPRINT",EDGE,{"derivedFrom":sQuery(id+"F0.wireOp",EDGE,"E12.MirrorC")}),-1.0]])]});
            var Q1;
            Q1=makeQuery(id+"F0.imprint","IMPRINT",FACE,{"disambiguationData":[TD([[makeQuery(id+"F0.imprint","IMPRINT",EDGE,{"derivedFrom":sQuery(id+"F0.wireOp",EDGE,"E11.MirrorC")}),1.0]])]});
            extrude(context, id + "F31", {"entities" : qUnion([Q0, Q1]), "operationType" : NewBodyOperationType.REMOVE, "depth" : 15 * mm});
        }
        {
            var Q0;
            {var subQ0=sQuery(id+"F2.wireOp",EDGE,"E13.right");Q0=makeQuery(id+"F25.boolean.opBoolean","MERGE",FACE,{"derivedFrom":[makeQuery(id+"F14.boolean.opBoolean","MERGE",FACE,{"derivedFrom":[makeQuery(id+"F11.opExtrude","SWEPT_FACE",FACE,{"disambiguationData":[OSD([sQuery(id+"F10.wireOp",EDGE,"E60.right")])]}),makeQuery(id+"F14.opExtrude","SWEPT_FACE",FACE,{"disambiguationData":[OSD([sQuery(id+"F13.wireOp",EDGE,"E112.right")])]})]}),makeQuery(id+"F23.boolean.opBoolean","MERGE",FACE,{"derivedFrom":[makeQuery(id+"F4.boolean.opBoolean","MERGE",FACE,{"derivedFrom":[makeQuery(id+"F3.opExtrude","SWEPT_FACE",FACE,{"disambiguationData":[OSD([subQ0])]}),makeQuery(id+"F4.opExtrude","SWEPT_FACE",FACE,{"disambiguationData":[OSD([subQ0])]})]}),makeQuery(id+"F23.opExtrude","SWEPT_FACE",FACE,{"disambiguationData":[OSD([sQuery(id+"F22.wireOp",EDGE,"E165.left")])]})]}),makeQuery(id+"F25.opExtrude","SWEPT_FACE",FACE,{"disambiguationData":[OSD([sQuery(id+"F24.wireOp",EDGE,"E168.left")])]})]});}
            var sketch = newSketch(context, id + "F32", { "sketchPlane" : qUnion([Q0])});
            skLineSegment(sketch, "E174.bottom", {"start": v(4, 5) * mm, "end": v(-33, 5) * mm, "construction": true});
            skLineSegment(sketch, "E174.top", {"start": v(4, -44) * mm, "end": v(-33, -44) * mm, "construction": true});
            skLineSegment(sketch, "E174.left", {"start": v(4, 5) * mm, "end": v(4, -44) * mm, "construction": true});
            skLineSegment(sketch, "E174.right", {"start": v(-33, 5) * mm, "end": v(-33, -44) * mm, "construction": true});
            skCircle(sketch, "E175", {"center": v(-33, -19.5) * mm, "radius": 19 * mm});
            skSolve(sketch);
        }
        {
            var Q0;
            Q0 = qSketchRegion(id + "F32", true);
            extrude(context, id + "F33", {"entities" : qUnion([Q0]), "operationType" : NewBodyOperationType.REMOVE, "oppositeDirection" : true, "depth" : 74 * mm});
        }
        {
            var Q0;
            {var subQ0=sQuery(id+"F2.wireOp",EDGE,"E13.bottom");Q0=makeQuery(id+"F4.boolean.opBoolean","MERGE",FACE,{"derivedFrom":[makeQuery(id+"F3.opExtrude","SWEPT_FACE",FACE,{"disambiguationData":[OSD([subQ0])]}),makeQuery(id+"F4.opExtrude","SWEPT_FACE",FACE,{"disambiguationData":[OSD([subQ0])]})]});}
            var sketch = newSketch(context, id + "F34", { "sketchPlane" : qUnion([Q0])});
            skLineSegment(sketch, "E176.trimOffspring", {"start": v(-34.6, 3.78) * mm, "end": v(-33.39, 3.78) * mm});
            skLineSegment(sketch, "E177", {"start": v(-36.39, 5) * mm, "end": v(-34.6, 5) * mm});
            skLineSegment(sketch, "E178.MirrorCS", {"start": v(-31.6, 5) * mm, "end": v(-33.39, 5) * mm});
            skLineSegment(sketch, "E179.MirrorCS", {"start": v(-30.39, 5) * mm, "end": v(-28.6, 5) * mm});
            skLineSegment(sketch, "E180.MirrorCS", {"start": v(-25.6, 5) * mm, "end": v(-27.39, 5) * mm});
            skLineSegment(sketch, "E181.MirrorCS", {"start": v(-24.39, 5) * mm, "end": v(-22.6, 5) * mm});
            skPoint(sketch, "E182.end.orphan", {"position": v(-25.62, 7.45) * mm});
            skPoint(sketch, "E183.end.orphan", {"position": v(-32.5, 5) * mm});
            skLineSegment(sketch, "E184", {"start": v(-22.6, 5) * mm, "end": v(-24.39, 5) * mm, "construction": true});
            skLineSegment(sketch, "E185.MirrorCS", {"start": v(-22.6, 6.22) * mm, "end": v(-22, 6.22) * mm});
            skLineSegment(sketch, "E186.MirrorCS", {"start": v(-37, 6.22) * mm, "end": v(-36.39, 6.22) * mm});
            skLineSegment(sketch, "E187.MirrorCS", {"start": v(-25.6, 6.22) * mm, "end": v(-24.39, 6.22) * mm});
            skLineSegment(sketch, "E188.MirrorCS", {"start": v(-28.6, 6.22) * mm, "end": v(-27.39, 6.22) * mm});
            skLineSegment(sketch, "E189.MirrorCS", {"start": v(-34.6, 6.22) * mm, "end": v(-33.39, 6.22) * mm});
            skLineSegment(sketch, "E190.MirrorCS", {"start": v(-22, 7.4) * mm, "end": v(-37, 7.4) * mm});
            skLineSegment(sketch, "E191.MirrorCS", {"start": v(-22, 7.4) * mm, "end": v(-22, 6.22) * mm});
            skPoint(sketch, "E192.MirrorP", {"position": v(-25.62, 2.55) * mm});
            skLineSegment(sketch, "E193.MirrorCS", {"start": v(-31.6, 6.22) * mm, "end": v(-30.39, 6.22) * mm});
            skLineSegment(sketch, "E194.MirrorCS", {"start": v(-37, 7.4) * mm, "end": v(-37, 6.22) * mm});
            skLineSegment(sketch, "E195.MirrorCS", {"start": v(-22.6, 6.22) * mm, "end": v(-22.6, 5) * mm});
            skLineSegment(sketch, "E196.MirrorCS", {"start": v(-24.39, 6.22) * mm, "end": v(-24.39, 5) * mm});
            skLineSegment(sketch, "E197.MirrorCS", {"start": v(-25.6, 6.22) * mm, "end": v(-25.6, 5) * mm});
            skLineSegment(sketch, "E198.MirrorCS", {"start": v(-27.39, 6.22) * mm, "end": v(-27.39, 5) * mm});
            skLineSegment(sketch, "E199.MirrorCS", {"start": v(-28.6, 6.22) * mm, "end": v(-28.6, 5) * mm});
            skLineSegment(sketch, "E200.MirrorCS", {"start": v(-30.39, 6.22) * mm, "end": v(-30.39, 5) * mm});
            skLineSegment(sketch, "E201.MirrorCS", {"start": v(-33.39, 6.22) * mm, "end": v(-33.39, 5) * mm});
            skLineSegment(sketch, "E202.MirrorCS", {"start": v(-34.6, 6.22) * mm, "end": v(-34.6, 5) * mm});
            skLineSegment(sketch, "E203.MirrorCS", {"start": v(-36.39, 6.22) * mm, "end": v(-36.39, 5) * mm});
            skLineSegment(sketch, "E204.MirrorCS", {"start": v(-31.6, 6.22) * mm, "end": v(-31.6, 5) * mm});
            skPoint(sketch, "E205.end.orphan", {"position": v(-36.39, 3.78) * mm});
            skPoint(sketch, "E205.start.orphan", {"position": v(-37, 3.78) * mm});
            skPoint(sketch, "E206.end.orphan", {"position": v(-37, 2.6) * mm});
            skPoint(sketch, "E207.start.orphan", {"position": v(-22, 2.6) * mm});
            skPoint(sketch, "E208.trimOffspring.end.orphan", {"position": v(-22, 3.78) * mm});
            skPoint(sketch, "E209.MirrorCS.end.orphan", {"position": v(-22.6, 5) * mm});
            skPoint(sketch, "E209.MirrorCS.start.orphan", {"position": v(-22.6, 3.78) * mm});
            skPoint(sketch, "E210.MirrorCS.end.orphan", {"position": v(-24.39, 5) * mm});
            skPoint(sketch, "E211.MirrorCS.end.orphan", {"position": v(-25.6, 5) * mm});
            skPoint(sketch, "E212.MirrorCS.end.orphan", {"position": v(-27.39, 5) * mm});
            skPoint(sketch, "E213.MirrorCS.end.orphan", {"position": v(-28.6, 5) * mm});
            skPoint(sketch, "E214.trimOffspring.end.orphan", {"position": v(-27.39, 3.78) * mm});
            skPoint(sketch, "E214.trimOffspring.start.orphan", {"position": v(-28.6, 3.78) * mm});
            skPoint(sketch, "E215.orphan", {"position": v(-25.6, 3.78) * mm});
            skPoint(sketch, "E216.trimOffspring.end.orphan", {"position": v(-24.39, 3.78) * mm});
            skPoint(sketch, "E217.MirrorCS.end.orphan", {"position": v(-30.39, 5) * mm});
            skPoint(sketch, "E218.MirrorCS.end.orphan", {"position": v(-31.6, 5) * mm});
            skPoint(sketch, "E219.trimOffspring.end.orphan", {"position": v(-30.39, 3.78) * mm});
            skPoint(sketch, "E219.trimOffspring.start.orphan", {"position": v(-31.6, 3.78) * mm});
            skPoint(sketch, "E220.MirrorCS.end.orphan", {"position": v(-33.39, 5) * mm});
            skLineSegment(sketch, "E221.trimOffspring", {"start": v(-25.6, 5) * mm, "end": v(-27.39, 5) * mm, "construction": true});
            skPoint(sketch, "E222.orphan", {"position": v(-22, 5) * mm});
            skLineSegment(sketch, "E223.trimOffspring", {"start": v(-28.6, 5) * mm, "end": v(-30.39, 5) * mm, "construction": true});
            skLineSegment(sketch, "E224.trimOffspring", {"start": v(-31.6, 5) * mm, "end": v(-33.39, 5) * mm, "construction": true});
            skLineSegment(sketch, "E225.trimOffspring", {"start": v(-34.6, 5) * mm, "end": v(-36.39, 5) * mm, "construction": true});
            skSolve(sketch);
        }
        {
            var Q0;
            Q0=makeQuery(id+"F34.imprint","IMPRINT",FACE,{"disambiguationData":[TD([[makeQuery(id+"F34.imprint","IMPRINT",EDGE,{"derivedFrom":sQuery(id+"F34.wireOp",EDGE,"E177")}),1.0]])]});
            extrude(context, id + "F35", {"entities" : qUnion([Q0]), "operationType" : NewBodyOperationType.REMOVE, "oppositeDirection" : true, "depth" : 10 * mm});
        }
        {
            var Q0;
            Q0=qCreatedBy(makeId("Top.planeOp"),FACE);
            var sketch = newSketch(context, id + "F36", { "sketchPlane" : qUnion([Q0])});
            skLineSegment(sketch, "E226.bottom", {"start": v(-22, 55) * mm, "end": v(-37, 55) * mm});
            skLineSegment(sketch, "E226.top", {"start": v(-22, 4) * mm, "end": v(-37, 4) * mm});
            skLineSegment(sketch, "E226.left", {"start": v(-22, 55) * mm, "end": v(-22, 4) * mm});
            skLineSegment(sketch, "E226.right", {"start": v(-37, 55) * mm, "end": v(-37, 4) * mm});
            skLineSegment(sketch, "E227.MirrorCS", {"start": v(22, 55) * mm, "end": v(37, 55) * mm});
            skLineSegment(sketch, "E228.MirrorCS", {"start": v(37, 55) * mm, "end": v(37, 4) * mm});
            skLineSegment(sketch, "E229.MirrorCS", {"start": v(22, 4) * mm, "end": v(37, 4) * mm});
            skLineSegment(sketch, "E230.MirrorCS", {"start": v(22, 55) * mm, "end": v(22, 4) * mm});
            skLineSegment(sketch, "E231.bottom", {"start": v(-37, -33) * mm, "end": v(-22, -33) * mm});
            skLineSegment(sketch, "E231.top", {"start": v(-37, -55) * mm, "end": v(-22, -55) * mm});
            skLineSegment(sketch, "E231.left", {"start": v(-37, -33) * mm, "end": v(-37, -55) * mm});
            skLineSegment(sketch, "E231.right", {"start": v(-22, -33) * mm, "end": v(-22, -55) * mm});
            skLineSegment(sketch, "E232.MirrorCS", {"start": v(37, -33) * mm, "end": v(37, -55) * mm});
            skLineSegment(sketch, "E233.MirrorCS", {"start": v(37, -33) * mm, "end": v(22, -33) * mm});
            skLineSegment(sketch, "E234.MirrorCS", {"start": v(22, -33) * mm, "end": v(22, -55) * mm});
            skLineSegment(sketch, "E235.MirrorCS", {"start": v(37, -55) * mm, "end": v(22, -55) * mm});
            skSolve(sketch);
        }
        {
            var Q0;
            Q0 = qSketchRegion(id + "F36", true);
            extrude(context, id + "F37", {"entities" : qUnion([Q0]), "operationType" : NewBodyOperationType.ADD, "depth" : 5 * mm});
        }
        {
            var Q0;
            Q0=makeQuery(id+"F37.opExtrude","SWEPT_EDGE",EDGE,{"disambiguationData":[OSD([sQuery(id+"F36.wireOp",EDGE,"E231.top"),sQuery(id+"F36.wireOp",EDGE,"E231.left")])]});
            var Q1;
            Q1=makeQuery(id+"F37.opExtrude","SWEPT_EDGE",EDGE,{"disambiguationData":[OSD([sQuery(id+"F36.wireOp",EDGE,"E232.MirrorCS"),sQuery(id+"F36.wireOp",EDGE,"E235.MirrorCS")])]});
            var Q2;
            Q2=makeQuery(id+"F37.opExtrude","SWEPT_EDGE",EDGE,{"disambiguationData":[OSD([sQuery(id+"F36.wireOp",EDGE,"E227.MirrorCS"),sQuery(id+"F36.wireOp",EDGE,"E228.MirrorCS")])]});
            var Q3;
            Q3=makeQuery(id+"F37.opExtrude","SWEPT_EDGE",EDGE,{"disambiguationData":[OSD([sQuery(id+"F36.wireOp",EDGE,"E226.bottom"),sQuery(id+"F36.wireOp",EDGE,"E226.right")])]});
            fillet(context, id + "F38", {"entities" : qUnion([Q0, Q1, Q2, Q3]), "radius" : 20 * mm, "tangentPropagation" : true, "allowEdgeOverflow" : false});
        }
    });
